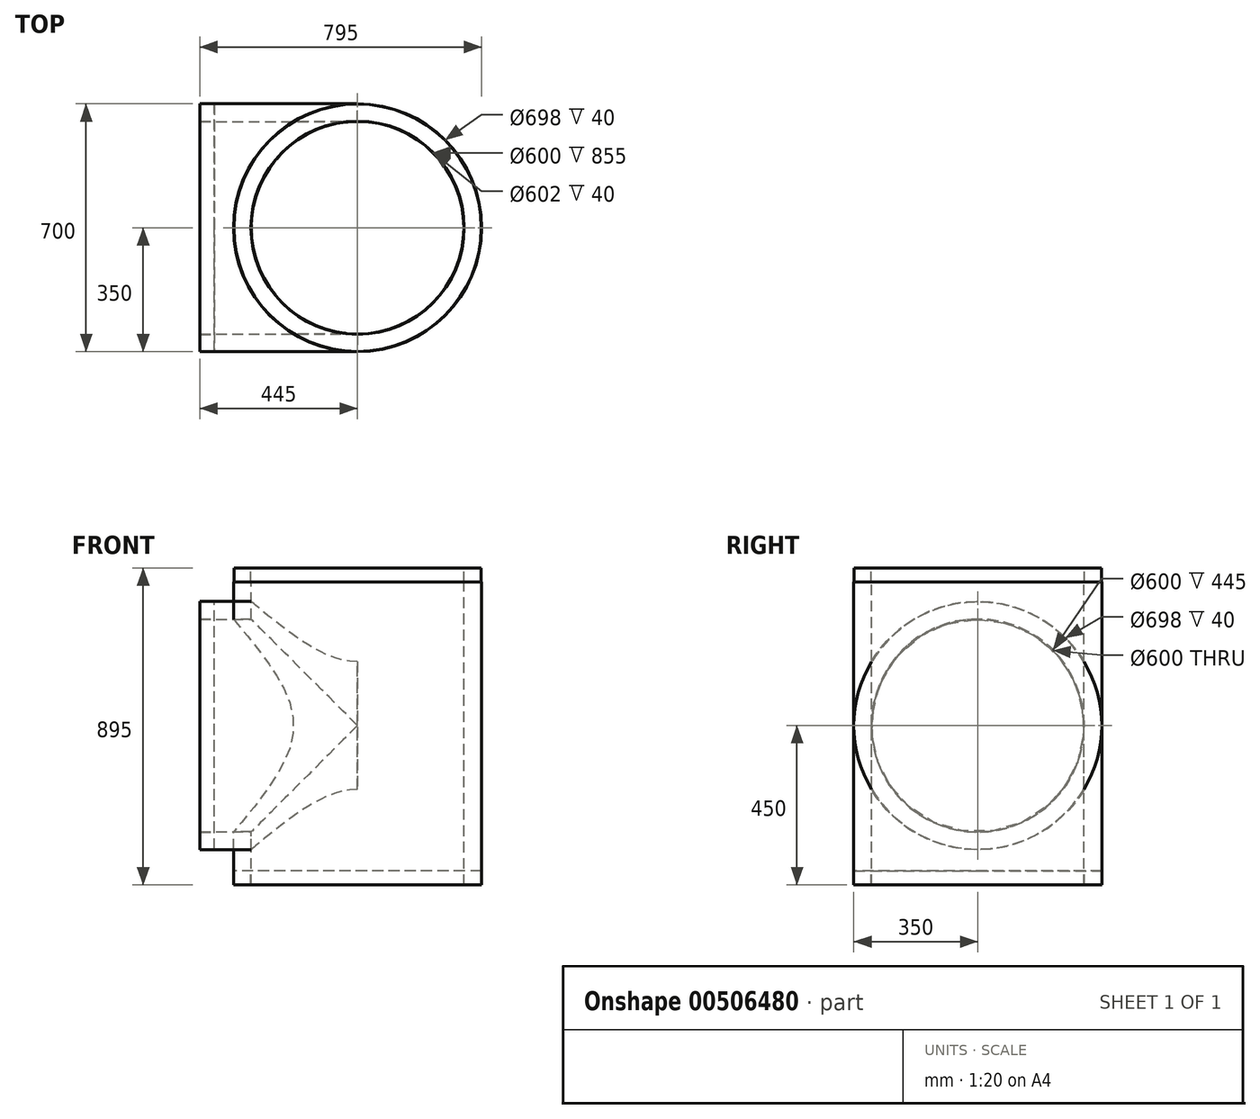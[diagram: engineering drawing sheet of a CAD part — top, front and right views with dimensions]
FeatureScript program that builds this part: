
annotation { "Feature Type Name" : "Feature", "Feature Type Description" : "" }
export const myFeature = defineFeature(function(context is Context, id is Id, definition is map)
    precondition{}
    {
        {
            var Q0;
            Q0=qCreatedBy(makeId("Front.planeOp"),FACE);
            var sketch = newSketch(context, id + "F0", { "sketchPlane" : qUnion([Q0])});
            skLineSegment(sketch, "E0", {"start": v(0, 722.18) * mm, "end": v(0, -793.11) * mm, "construction": true});
            skLineSegment(sketch, "E1", {"start": v(-300, -450) * mm, "end": v(-300, 405) * mm});
            skLineSegment(sketch, "E2", {"start": v(-300, 405) * mm, "end": v(-301, 405) * mm});
            skLineSegment(sketch, "E3", {"start": v(-301, 405) * mm, "end": v(-301, 445) * mm});
            skLineSegment(sketch, "E4", {"start": v(-301, 445) * mm, "end": v(-349, 445) * mm});
            skLineSegment(sketch, "E5", {"start": v(-349, 445) * mm, "end": v(-349, 405) * mm});
            skLineSegment(sketch, "E6", {"start": v(-349, 405) * mm, "end": v(-350, 405) * mm});
            skLineSegment(sketch, "E7", {"start": v(-350, 405) * mm, "end": v(-350, -450) * mm});
            skLineSegment(sketch, "E8", {"start": v(-350, -450) * mm, "end": v(-349, -450) * mm});
            skLineSegment(sketch, "E9", {"start": v(-349, -450) * mm, "end": v(-349, -410) * mm});
            skLineSegment(sketch, "E10", {"start": v(-349, -410) * mm, "end": v(-301, -410) * mm});
            skLineSegment(sketch, "E11", {"start": v(-301, -410) * mm, "end": v(-301, -450) * mm});
            skLineSegment(sketch, "E12", {"start": v(-301, -450) * mm, "end": v(-300, -450) * mm});
            skLineSegment(sketch, "E13", {"start": v(0, 0) * mm, "end": v(-528, 0) * mm, "construction": true});
            skLineSegment(sketch, "E14", {"start": v(0, -300) * mm, "end": v(-445, -300) * mm});
            skLineSegment(sketch, "E15", {"start": v(-445, -350) * mm, "end": v(0, -350) * mm});
            skLineSegment(sketch, "E16", {"start": v(0, -350) * mm, "end": v(0, -300) * mm});
            skLineSegment(sketch, "E17", {"start": v(-445, -300) * mm, "end": v(-445, -301) * mm});
            skLineSegment(sketch, "E18", {"start": v(-405, -301) * mm, "end": v(-445, -301) * mm});
            skLineSegment(sketch, "E19", {"start": v(-405, -301) * mm, "end": v(-405, -349) * mm});
            skLineSegment(sketch, "E20", {"start": v(-445, -349) * mm, "end": v(-405, -349) * mm});
            skLineSegment(sketch, "E21", {"start": v(-445, -349) * mm, "end": v(-445, -350) * mm});
            skSolve(sketch);
        }
        {
            var Q0;
            {var subQ0=sQuery(id+"F0.wireOp",EDGE,"E2");Q0=makeQuery(id+"F0.imprint","IMPRINT",FACE,{"disambiguationData":[TD([[makeQuery(id+"F0.imprint","IMPRINT",EDGE,{"derivedFrom":subQ0}),1.0]])]});}
            var Q1;
            {var subQ0=sQuery(id+"F0.wireOp",EDGE,"E15");var subQ1=sQuery(id+"F0.wireOp",EDGE,"E1");var subQ2=makeQuery(id+"F0.imprint","INTERSECT",VERTEX,{"derivedFrom":[subQ1,subQ0]});Q1=makeQuery(id+"F0.imprint","IMPRINT",FACE,{"disambiguationData":[TD([[makeQuery(id+"F0.imprint","IMPRINT",EDGE,{"disambiguationData":[TD([[subQ2,-1.0]])],"derivedFrom":subQ1}),1.0]])]});}
            var Q2;
            {var subQ0=sQuery(id+"F0.wireOp",EDGE,"E8");Q2=makeQuery(id+"F0.imprint","IMPRINT",FACE,{"disambiguationData":[TD([[makeQuery(id+"F0.imprint","IMPRINT",EDGE,{"derivedFrom":subQ0}),1.0]])]});}
            var Q3;
            Q3=sQuery(id+"F0.wireOp",EDGE,"E0");
            revolve(context, id + "F1", {"entities" : qUnion([Q0, Q1, Q2]), "axis" : qUnion([Q3]), "revolveType" : RevolveType.FULL});
        }
        {
            var Q0;
            {var subQ0=sQuery(id+"F0.wireOp",EDGE,"E17");Q0=makeQuery(id+"F0.imprint","IMPRINT",FACE,{"disambiguationData":[TD([[makeQuery(id+"F0.imprint","IMPRINT",EDGE,{"derivedFrom":subQ0}),1.0]])]});}
            var Q1;
            {var subQ5=sQuery(id+"F0.wireOp",EDGE,"E16");Q1=makeQuery(id+"F0.imprint","IMPRINT",FACE,{"disambiguationData":[TD([[makeQuery(id+"F0.imprint","IMPRINT",EDGE,{"derivedFrom":subQ5}),1.0]])]});}
            var Q2;
            {var subQ0=sQuery(id+"F0.wireOp",EDGE,"E15");var subQ1=sQuery(id+"F0.wireOp",EDGE,"E1");var subQ2=makeQuery(id+"F0.imprint","INTERSECT",VERTEX,{"derivedFrom":[subQ1,subQ0]});Q2=makeQuery(id+"F0.imprint","IMPRINT",FACE,{"disambiguationData":[TD([[makeQuery(id+"F0.imprint","IMPRINT",EDGE,{"disambiguationData":[TD([[subQ2,-1.0]])],"derivedFrom":subQ1}),1.0]])]});}
            var Q3;
            Q3=sQuery(id+"F0.wireOp",EDGE,"E13");
            revolve(context, id + "F2", {"surfaceOperationType" : NewSurfaceOperationType.NEW, "entities" : qUnion([Q0, Q1, Q2]), "axis" : qUnion([Q3]), "revolveType" : RevolveType.FULL});
        }
        {
            var Q0;
            Q0=makeQuery(id+"F2.opRevolve","SWEPT_FACE",FACE,{"disambiguationData":[OSD([sQuery(id+"F0.wireOp",EDGE,"E19")])]});
            var sketch = newSketch(context, id + "F3", { "sketchPlane" : qUnion([Q0])});
            skCircle(sketch, "E22.0", {"center": v(0, 0) * mm, "radius": 300 * mm});
            skSolve(sketch);
        }
        {
            var Q0;
            Q0=qSketchRegion(id+"F3",true);
            var Q1;
            Q1=makeQuery(id+"F2.opRevolve","SWEPT_FACE",FACE,{"disambiguationData":[OSD([sQuery(id+"F0.wireOp",EDGE,"E16")])]});
            extrude(context, id + "F4", {"entities" : qUnion([Q0]), "operationType" : NewBodyOperationType.REMOVE, "endBound" : BoundingType.UP_TO_SURFACE, "oppositeDirection" : true, "depth" : 25 * mm, "endBoundEntityFace" : qUnion([Q1]), "offsetDistance" : 25 * mm});
        }
        {
            var Q0;
            Q0=makeQuery(id+"F1.opRevolve","SWEPT_FACE",FACE,{"disambiguationData":[OSD([sQuery(id+"F0.wireOp",EDGE,"E4")])]});
            var sketch = newSketch(context, id + "F5", { "sketchPlane" : qUnion([Q0])});
            skCircle(sketch, "E23", {"center": v(0, 0) * mm, "radius": 300 * mm});
            skSolve(sketch);
        }
        {
            var Q0;
            Q0=qSketchRegion(id+"F5",true);
            extrude(context, id + "F6", {"entities" : qUnion([Q0]), "operationType" : NewBodyOperationType.REMOVE, "oppositeDirection" : true, "depth" : 1200 * mm});
        }
    });
